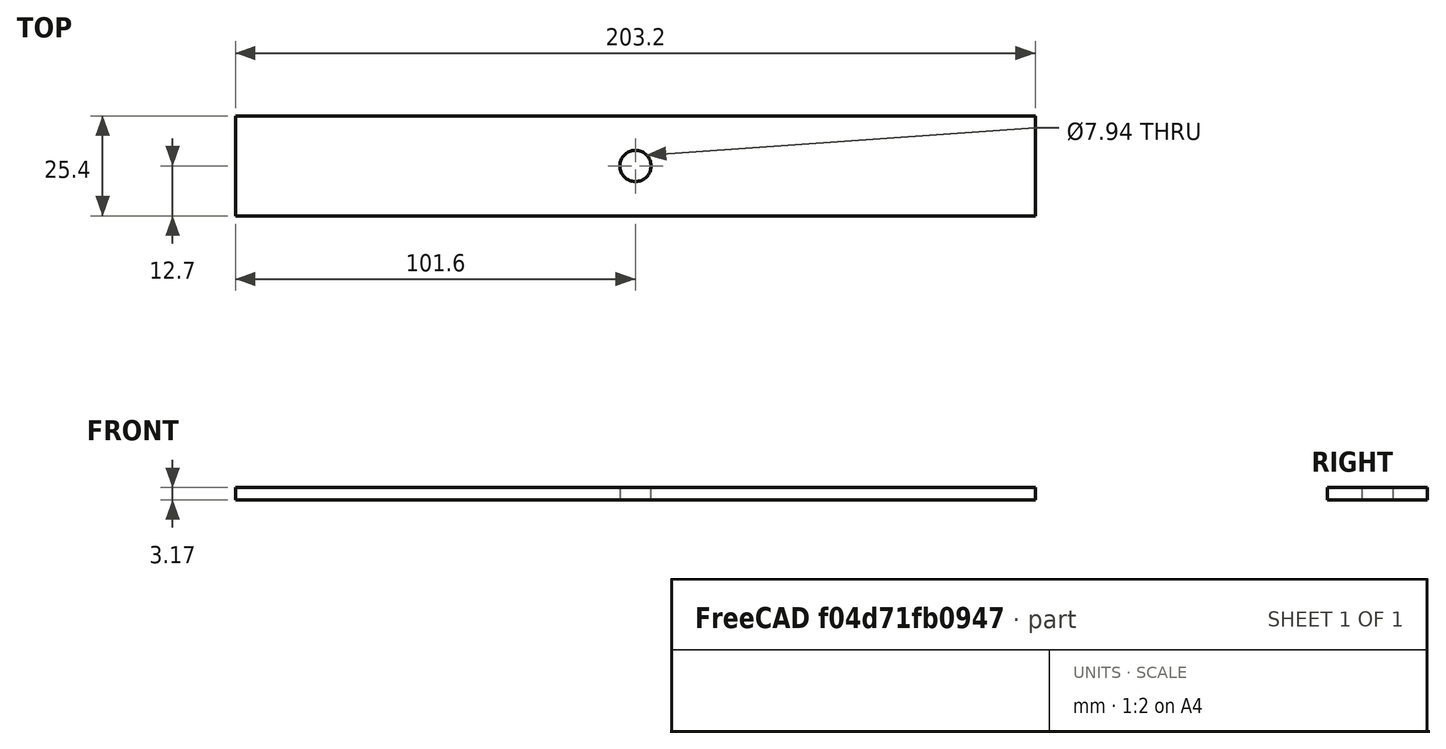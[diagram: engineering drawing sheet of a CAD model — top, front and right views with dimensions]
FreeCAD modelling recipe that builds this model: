
FCSTD DOCUMENT  (FreeCAD 0.17R13522 (Git))
Label: weapon
License: All rights reserved
LicenseURL: http://en.wikipedia.org/wiki/All_rights_reserved
objects: Sketcher::SketchObject×1, PartDesign::Pad×1, PartDesign::Body×1
note: 4 computed .brp shape members not serialized (recipe doc carries the construction recipe); baked Part::Feature solids carry a one-line shape summary decoded from their .brp

FEATURE [Sketcher::SketchObject] Sketch
  MapMode = 5
  Support = -> [XY_Plane]
  sketch-geometry (5):
    g0: LineSegment StartX=-101.6 StartY=12.7 StartZ=0 EndX=101.6 EndY=12.7 EndZ=0
    g1: LineSegment StartX=101.6 StartY=12.7 StartZ=0 EndX=101.6 EndY=-12.7 EndZ=0
    g2: LineSegment StartX=101.6 StartY=-12.7 StartZ=0 EndX=-101.6 EndY=-12.7 EndZ=0
    g3: LineSegment StartX=-101.6 StartY=-12.7 StartZ=0 EndX=-101.6 EndY=12.7 EndZ=0
    g4: Circle CenterX=0 CenterY=0 CenterZ=0 NormalX=0 NormalY=0 NormalZ=1 AngleXU=0 Radius=3.96875
  constraints (13):
    c: Coincident(g0,g1)
    c: Coincident(g1,g2)
    c: Coincident(g2,g3)
    c: Coincident(g3,g0)
    c: Horizontal(g0)
    c: Horizontal(g2)
    c: Vertical(g1)
    c: Vertical(g3)
    c: DistanceY(g1,g1) = 25.4
    c: DistanceX(g0,g0) = 203.2
    c: Symmetric(g1,g0,g-1)
    c: Coincident(g4,g-1)
    c: Radius(g4) = 3.96875
FEATURE [PartDesign::Pad] Pad
  Length = 3.175
  Length2 = 99.9998
  Profile = -> Sketch
  Type = 0
FEATURE [PartDesign::Body] Body
  Group = -> [Sketch,Pad]
  Origin = -> Origin
  Tip = -> Pad
